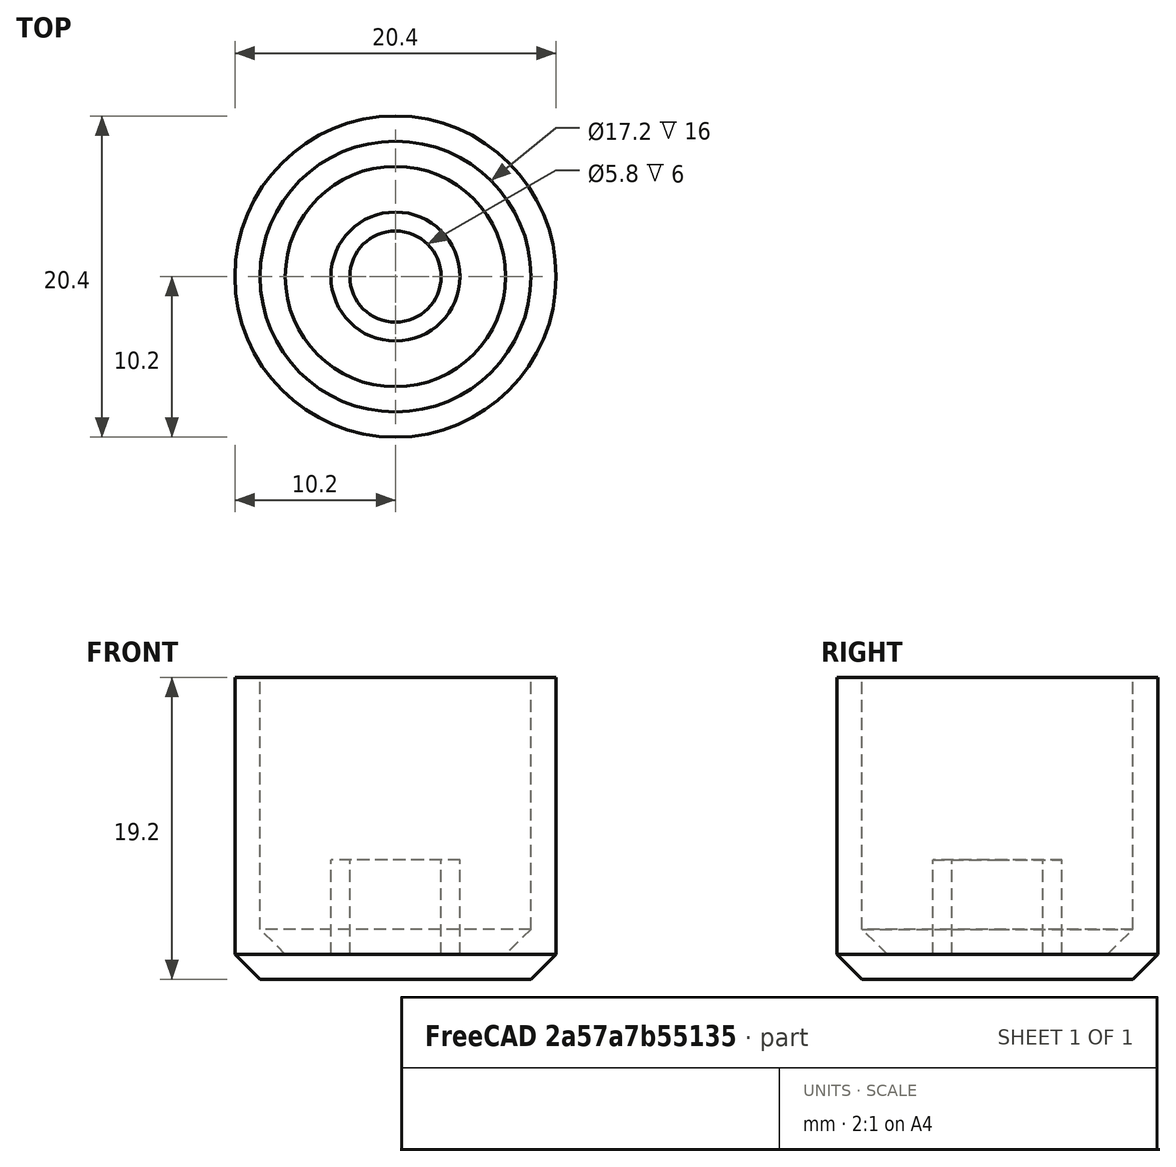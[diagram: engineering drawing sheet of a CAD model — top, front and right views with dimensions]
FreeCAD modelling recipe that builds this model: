
FCSTD DOCUMENT  (FreeCAD 0.16R)
Label: SolderingStationV2_knob
License: All rights reserved
LicenseURL: http://en.wikipedia.org/wiki/All_rights_reserved
objects: Part::Cylinder×4, Part::Cut×2, Part::Chamfer×1, Part::MultiFuse×1
note: 8 computed .brp shape members not serialized (recipe doc carries the construction recipe); baked Part::Feature solids carry a one-line shape summary decoded from their .brp

FEATURE [Part::Cylinder] Cylinder  label="Zylinder_außen"
  Angle = 360
  Height = 19.2
  Radius = 10.2
FEATURE [Part::Cylinder] Cylinder001  label="Zylinder_innen"
  Angle = 360
  Height = 17.6
  Placement = pos=(0,0,1.6) rot=(0,0,1;0rad)
  Radius = 8.6
FEATURE [Part::Cut] Cut  label="außen_roh"
  Base = -> Cylinder
  Tool = -> Cylinder001
FEATURE [Part::Chamfer] Chamfer  label="außen"
  Base = -> Cut
  Edges = 2 edges r=1.6: [Edge3,Edge6]
FEATURE [Part::Cylinder] Cylinder002  label="Shaft_außen"
  Angle = 360
  Height = 7.6
  Radius = 4.1
FEATURE [Part::Cylinder] Cylinder003  label="Shaft_innen"
  Angle = 360
  Height = 6
  Placement = pos=(0,0,1.6) rot=(0,0,1;0rad)
  Radius = 2.9
FEATURE [Part::Cut] Cut001  label="Shaft"
  Base = -> Cylinder002
  Tool = -> Cylinder003
FEATURE [Part::MultiFuse] Fusion  label="Knob"
  Shapes = -> [Chamfer,Cut001]
